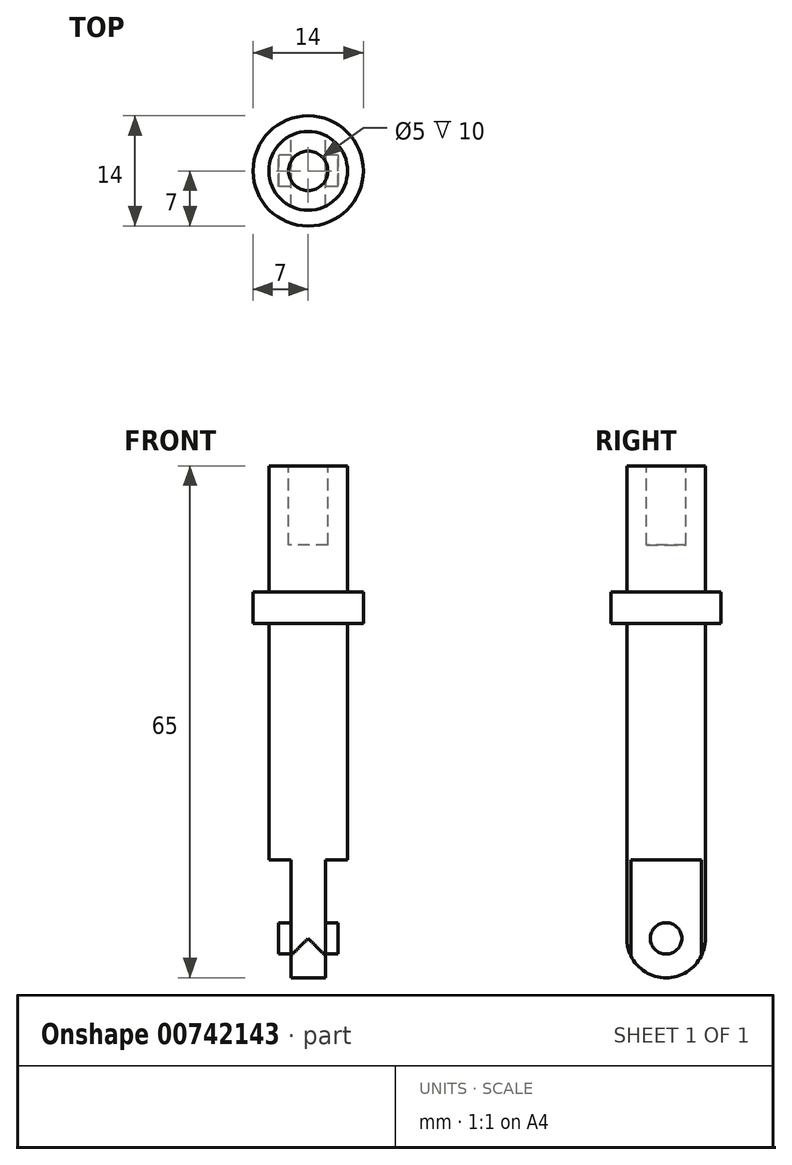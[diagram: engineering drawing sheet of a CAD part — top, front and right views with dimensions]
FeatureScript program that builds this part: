
annotation { "Feature Type Name" : "Feature", "Feature Type Description" : "" }
export const myFeature = defineFeature(function(context is Context, id is Id, definition is map)
    precondition{}
    {
        {
            var Q0;
            Q0=qCreatedBy(makeId("Top.planeOp"),FACE);
            var sketch = newSketch(context, id + "F0", { "sketchPlane" : qUnion([Q0])});
            skCircle(sketch, "E0", {"center": v(0, 0) * mm, "radius": 5 * mm});
            skSolve(sketch);
        }
        {
            var Q0;
            Q0=qSketchRegion(id+"F0",true);
            extrude(context, id + "F1", {"entities" : qUnion([Q0]), "depth" : 50 * mm, "offsetDistance" : 25 * mm});
        }
        {
            var Q0;
            Q0=makeQuery(id+"F1.opExtrude","CAP_FACE",FACE,{"disambiguationData":[OSD([sQuery(id+"F0.wireOp",EDGE,"E0")])],"isStart":true});
            var sketch = newSketch(context, id + "F2", { "sketchPlane" : qUnion([Q0])});
            skLineSegment(sketch, "E1.bottom", {"start": v(-2.2, 5) * mm, "end": v(2.2, 5) * mm});
            skLineSegment(sketch, "E1.top", {"start": v(-2.2, -5) * mm, "end": v(2.2, -5) * mm});
            skLineSegment(sketch, "E1.left", {"start": v(-2.2, 5) * mm, "end": v(-2.2, -5) * mm});
            skLineSegment(sketch, "E1.right", {"start": v(2.2, 5) * mm, "end": v(2.2, -5) * mm});
            skSolve(sketch);
        }
        {
            var Q0;
            {var subQ0=makeQuery(id+"F1.opExtrude","CAP_EDGE",EDGE,{"disambiguationData":[OSD([sQuery(id+"F0.wireOp",EDGE,"E0")])],"isStart":true});var subQ2=sQuery(id+"F2.wireOp",EDGE,"E1.left");var subQ3=makeQuery(id+"F2.imprint","INTERSECT",VERTEX,{"disambiguationData":[OD(0.0)],"derivedFrom":[subQ0,subQ2]});Q0=makeQuery(id+"F2.imprint","IMPRINT",FACE,{"disambiguationData":[TD([[makeQuery(id+"F2.imprint","IMPRINT",EDGE,{"disambiguationData":[TD([[subQ3,-1.0]])],"derivedFrom":subQ2}),1.0]])]});}
            extrude(context, id + "F3", {"entities" : qUnion([Q0]), "operationType" : NewBodyOperationType.ADD, "depth" : 15 * mm, "offsetDistance" : 25 * mm});
        }
        {
            var Q0;
            Q0=makeQuery(id+"F3.opExtrude","SWEPT_FACE",FACE,{"disambiguationData":[OSD([sQuery(id+"F2.wireOp",EDGE,"E1.right")])]});
            var sketch = newSketch(context, id + "F4", { "sketchPlane" : qUnion([Q0])});
            skCircle(sketch, "E2", {"center": v(0, -10) * mm, "radius": 5 * mm});
            skLineSegment(sketch, "E3", {"start": v(0, -10) * mm, "end": v(0, -15) * mm, "construction": true});
            skLineSegment(sketch, "E4", {"start": v(5, -10) * mm, "end": v(5, -15) * mm});
            skLineSegment(sketch, "E5", {"start": v(5, -15) * mm, "end": v(-5, -15) * mm});
            skLineSegment(sketch, "E6", {"start": v(-5, -15) * mm, "end": v(-5, -10) * mm});
            skSolve(sketch);
        }
        {
            var Q0;
            {var subQ0=sQuery(id+"F4.wireOp",EDGE,"E4");Q0=makeQuery(id+"F4.imprint","IMPRINT",FACE,{"disambiguationData":[TD([[makeQuery(id+"F4.imprint","IMPRINT",EDGE,{"derivedFrom":subQ0}),-1.0]])]});}
            var Q1;
            {var subQ0=sQuery(id+"F4.wireOp",EDGE,"E5");var subQ1=sQuery(id+"F4.wireOp",EDGE,"E2");var subQ2=makeQuery(id+"F4.imprint","INTERSECT",VERTEX,{"derivedFrom":[subQ1,subQ0]});Q1=makeQuery(id+"F4.imprint","IMPRINT",FACE,{"disambiguationData":[TD([[makeQuery(id+"F4.imprint","IMPRINT",EDGE,{"disambiguationData":[TD([[subQ2,-1.0]])],"derivedFrom":subQ1}),-1.0]])]});}
            var Q2;
            {var subQ0=sQuery(id+"F4.wireOp",EDGE,"E5");var subQ1=sQuery(id+"F4.wireOp",EDGE,"E2");var subQ2=makeQuery(id+"F4.imprint","INTERSECT",VERTEX,{"derivedFrom":[subQ1,subQ0]});Q2=makeQuery(id+"F4.imprint","IMPRINT",FACE,{"disambiguationData":[TD([[makeQuery(id+"F4.imprint","IMPRINT",EDGE,{"disambiguationData":[TD([[subQ2,1.0]])],"derivedFrom":subQ1}),-1.0]])]});}
            var Q3;
            {var subQ0=sQuery(id+"F4.wireOp",EDGE,"E6");Q3=makeQuery(id+"F4.imprint","IMPRINT",FACE,{"disambiguationData":[TD([[makeQuery(id+"F4.imprint","IMPRINT",EDGE,{"derivedFrom":subQ0}),-1.0]])]});}
            extrude(context, id + "F5", {"entities" : qUnion([Q0, Q1, Q2, Q3]), "operationType" : NewBodyOperationType.REMOVE, "oppositeDirection" : true, "depth" : 25 * mm, "offsetDistance" : 25 * mm});
        }
        {
            var Q0;
            Q0=makeQuery(id+"F3.opExtrude","SWEPT_FACE",FACE,{"disambiguationData":[OSD([sQuery(id+"F2.wireOp",EDGE,"E1.right")])]});
            var sketch = newSketch(context, id + "F6", { "sketchPlane" : qUnion([Q0])});
            skCircle(sketch, "E7", {"center": v(0, -10) * mm, "radius": 2 * mm});
            skSolve(sketch);
        }
        {
            var Q0;
            Q0=makeQuery(id+"F6.imprint","IMPRINT",FACE,{"disambiguationData":[TD([[makeQuery(id+"F6.imprint","IMPRINT",EDGE,{"derivedFrom":sQuery(id+"F6.wireOp",EDGE,"E7")}),1.0]])]});
            extrude(context, id + "F7", {"entities" : qUnion([Q0]), "operationType" : NewBodyOperationType.ADD, "depth" : 1.6 * mm, "offsetDistance" : 25 * mm, "hasSecondDirection" : true, "secondDirectionOppositeDirection" : true, "secondDirectionDepth" : 6 * mm});
        }
        {
            var Q0;
            Q0=makeQuery(id+"F1.opExtrude","CAP_FACE",FACE,{"disambiguationData":[OSD([sQuery(id+"F0.wireOp",EDGE,"E0")])],"isStart":false});
            var sketch = newSketch(context, id + "F8", { "sketchPlane" : qUnion([Q0])});
            skCircle(sketch, "E8", {"center": v(0, 0) * mm, "radius": 2.5 * mm});
            skSolve(sketch);
        }
        {
            var Q0;
            Q0=makeQuery(id+"F8.imprint","IMPRINT",FACE,{"disambiguationData":[TD([[makeQuery(id+"F8.imprint","IMPRINT",EDGE,{"derivedFrom":sQuery(id+"F8.wireOp",EDGE,"E8")}),1.0]])]});
            extrude(context, id + "F9", {"entities" : qUnion([Q0]), "operationType" : NewBodyOperationType.REMOVE, "oppositeDirection" : true, "depth" : 10 * mm, "offsetDistance" : 25 * mm});
        }
        {
            var Q0;
            Q0=makeQuery(id+"F1.opExtrude","CAP_FACE",FACE,{"disambiguationData":[OSD([sQuery(id+"F0.wireOp",EDGE,"E0")])],"isStart":false});
            cPlane(context, id + "F10", {"entities" : qUnion([Q0]), "cplaneType" : CPlaneType.OFFSET, "offset" : 20 * mm, "oppositeDirection" : true, "width" : 150 * mm, "height" : 150 * mm});
        }
        {
            var Q0;
            Q0=qCreatedBy(id+"F10.planeOp",FACE);
            var sketch = newSketch(context, id + "F11", { "sketchPlane" : qUnion([Q0])});
            skCircle(sketch, "E9.0.0", {"center": v(0, 0) * mm, "radius": 5 * mm});
            skCircle(sketch, "E10", {"center": v(0, 0) * mm, "radius": 7 * mm});
            skSolve(sketch);
        }
        {
            var Q0;
            Q0=makeQuery(id+"F11.imprint","IMPRINT",FACE,{"disambiguationData":[TD([[makeQuery(id+"F11.imprint","IMPRINT",EDGE,{"derivedFrom":sQuery(id+"F11.wireOp",EDGE,"E9.0.0")}),-1.0]])]});
            extrude(context, id + "F12", {"entities" : qUnion([Q0]), "operationType" : NewBodyOperationType.ADD, "depth" : 4 * mm, "offsetDistance" : 25 * mm});
        }
    });
